# Revit family: svetilnik_alfresco_alkor_dku-01_os
name_source: partatom
category: Lighting Fixtures
revit_build: Autodesk Revit 2016 (Build: 20150506_1715(x64)
units: mm (PartAtom-declared; Revit-internal decimal feet)

## family parameters
Always vertical = Yes
Cut with Voids When Loaded = No
Light Source = No
Part Type = Normal
Room Calculation Point = No
Round Connector Dimension = Use Diameter
Shared = No
Work Plane-Based = No

## types (3) — shared parameters
ADSK_Единица измерения = шт
ADSK_Классификация нагрузок = Освещение
ADSK_Количество фаз = 2
ADSK_Количество фаз числовое = 2
ADSK_Коэффициент мощности = 0.97
ADSK_Масса = 43
ADSK_Модель = Алькор(ДТУ-01, ОССв)
ADSK_Напряжение = 220 V
ADSK_Размер_Высота = 4000 mm  [stored 13.1234 ft]
ADSK_Размер_Длина = 530 mm
ADSK_Размер_Ширина = 530 mm
ADSK_Ток = 0 A
ADSK_Энергоэффективность = 95 lm/W
IP Class = IP 65
Manufacturer = ALFRESCO
URL = http://www.allfresco.ru
Блок аварийного питания = No
Класс Защиты = 1
Класс пожароопасности = F (светильники предназначены для установки непосредственно на поверхность из нормально воспламеняемых матеоиалов)
Климатическая зона = У1
Область использования = Ландшафт, коттедж.поселки,микрорайоны,АЗС, автостоянки
Температура эксплуатации = -35 +40
Тип ИС = LED-светодиоды
Тип КСС = Asym
Тип ПРА = -
Тип продукции = Комплект(Опора освещения+LED светильник)
Угол положения светильника = 15.00°
Цветовая температура = 3000-5500

## per-type parameters (varying)
| type | ADSK_Артикул | ADSK_Наименование | ADSK_Номинальная мощность | ADSK_Полная мощность | Apparent Load | Световой поток_2 |
| Алькор-1(ОС) ДКУ 40Вт | 1105001320 | Алькор-1(ОС) ДКУ 40Вт - св-к Алькор ДКУ-01-AF (85х120, 02) на опоре ОС 3,9 ЧМ | 40 W | 41 VA | 41 VA | 3800 lm |
| Алькор-1(ОС) ДКУ 60Вт | 1105001330 | Алькор-1(ОС) ДКУ 60Вт - св-к Алькор ДКУ-01-AF (85х120, 02) на опоре ОС 3,9 ЧМ | 60 W | 62 VA | 62 VA | 5700 lm |
| Алькор-1(ОС) ДКУ 80Вт | 1105001340 | Алькор-1(ОС) ДКУ 80Вт - св-к Алькор ДКУ-01-AF (85х120, 02) на опоре ОС 3,9 ЧМ | 80 W | 82 VA | 82 VA | 7600 lm |

note: [stored X ft] marks values corroborated as IEEE doubles in the binary element streams (Revit-internal decimal feet)

## geometry (parser evidence)
native form markers: Blend x2
no freeform markers — native parametric forms only
